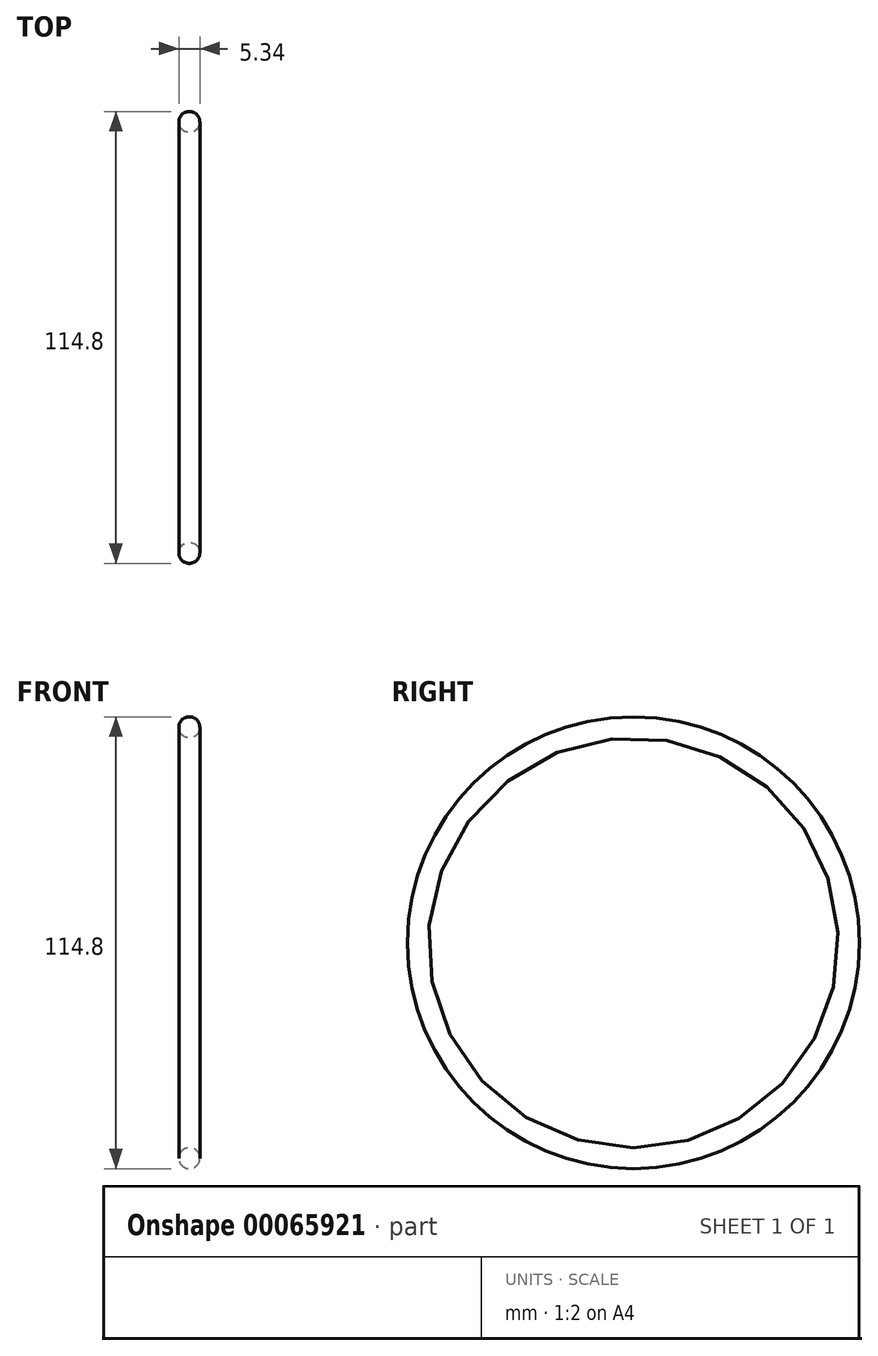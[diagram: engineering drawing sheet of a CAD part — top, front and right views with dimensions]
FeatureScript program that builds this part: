
annotation { "Feature Type Name" : "Feature", "Feature Type Description" : "" }
export const myFeature = defineFeature(function(context is Context, id is Id, definition is map)
    precondition{}
    {
        {
            var Q0;
            Q0=qCreatedBy(makeId("Front.planeOp"),FACE);
            var sketch = newSketch(context, id + "F0", { "sketchPlane" : qUnion([Q0])});
            skLineSegment(sketch, "E0", {"start": v(0, 0) * mm, "end": v(-6.06, 0) * mm, "construction": true});
            skCircle(sketch, "E1", {"center": v(0, 54.74) * mm, "radius": 2.67 * mm});
            skSolve(sketch);
        }
        {
            var Q0;
            Q0=makeQuery(id+"F0.imprint","IMPRINT",FACE,{"disambiguationData":[TD([[makeQuery(id+"F0.imprint","IMPRINT",EDGE,{"derivedFrom":sQuery(id+"F0.wireOp",EDGE,"E1")}),1.0]])]});
            var Q1;
            Q1=sQuery(id+"F0.wireOp",EDGE,"E0");
            revolve(context, id + "F1", {"entities" : qUnion([Q0]), "axis" : qUnion([Q1]), "revolveType" : RevolveType.FULL});
        }
    });
